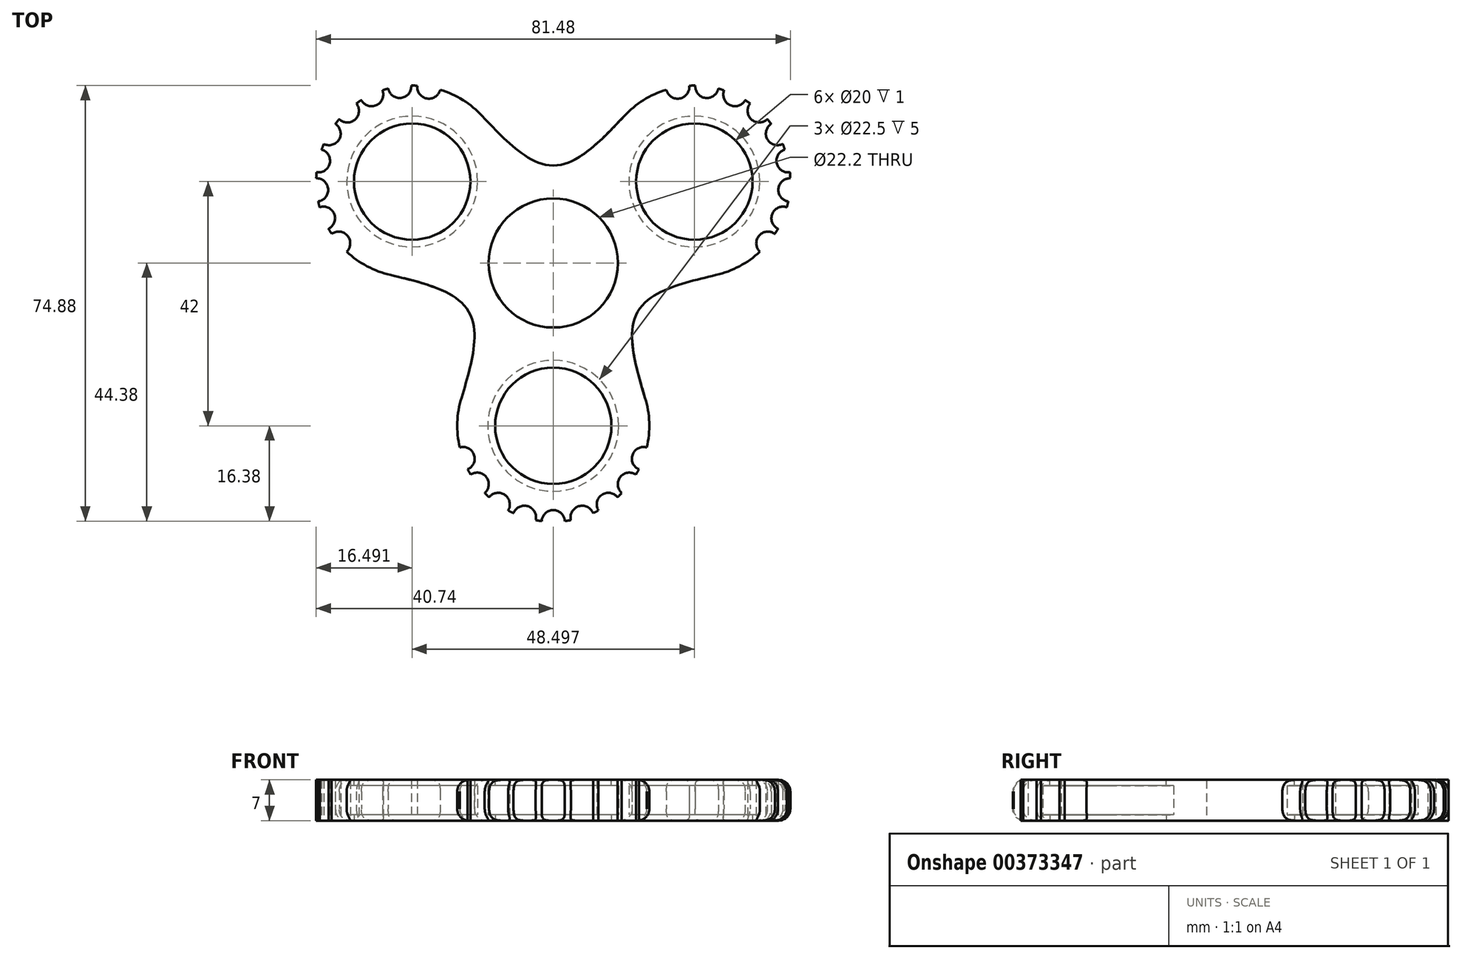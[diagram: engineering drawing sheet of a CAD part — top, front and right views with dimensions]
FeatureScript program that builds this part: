
annotation { "Feature Type Name" : "Feature", "Feature Type Description" : "" }
export const myFeature = defineFeature(function(context is Context, id is Id, definition is map)
    precondition{}
    {
        {
            var Q0;
            Q0=qCreatedBy(makeId("Top.planeOp"),FACE);
            var sketch = newSketch(context, id + "F0", { "sketchPlane" : qUnion([Q0])});
            skCircle(sketch, "E0", {"center": v(0, 0) * mm, "radius": 11.1 * mm});
            skCircle(sketch, "E1", {"center": v(-24.25, 14) * mm, "radius": 11.25 * mm});
            skCircle(sketch, "E2", {"center": v(24.25, 14) * mm, "radius": 11.25 * mm});
            skCircle(sketch, "E3", {"center": v(0, -28) * mm, "radius": 11.25 * mm});
            skLineSegment(sketch, "E4", {"start": v(-24.25, 14) * mm, "end": v(0, -28) * mm, "construction": true});
            skLineSegment(sketch, "E5", {"start": v(24.25, 14) * mm, "end": v(0, -28) * mm, "construction": true});
            skLineSegment(sketch, "E6", {"start": v(24.25, 14) * mm, "end": v(-24.25, 14) * mm, "construction": true});
            skLineSegment(sketch, "E7", {"start": v(0, 14) * mm, "end": v(0, 0) * mm, "construction": true});
            skLineSegment(sketch, "E8", {"start": v(0, 0) * mm, "end": v(12.12, -7) * mm, "construction": true});
            skLineSegment(sketch, "E9", {"start": v(0, 0) * mm, "end": v(-12.12, -7) * mm, "construction": true});
            skCircle(sketch, "E10", {"center": v(24.25, 14) * mm, "radius": 16.5 * mm});
            skCircle(sketch, "E11", {"center": v(-24.25, 14) * mm, "radius": 16.5 * mm});
            skCircle(sketch, "E12", {"center": v(0, -28) * mm, "radius": 16.5 * mm});
            skCircle(sketch, "E13", {"center": v(0, 0) * mm, "radius": 16.75 * mm, "construction": true});
            skLineSegment(sketch, "E14", {"start": v(-27.96, -2.08) * mm, "end": v(-15.78, -23.17) * mm, "construction": true});
            skLineSegment(sketch, "E15", {"start": v(15.78, -23.17) * mm, "end": v(27.96, -2.08) * mm, "construction": true});
            skLineSegment(sketch, "E16", {"start": v(12.18, 25.25) * mm, "end": v(-12.18, 25.25) * mm, "construction": true});
            skLineSegment(sketch, "E17", {"start": v(0, 0) * mm, "end": v(38.54, 22.25) * mm, "construction": true});
            skLineSegment(sketch, "E18", {"start": v(24.25, 14) * mm, "end": v(21.38, 30.25) * mm, "construction": true});
            skCircle(sketch, "E19", {"center": v(21.38, 30.25) * mm, "radius": 2 * mm});
            skCircle(sketch, "E20.1.0", {"center": v(26.4, 30.36) * mm, "radius": 2 * mm});
            skCircle(sketch, "E20.2.0", {"center": v(31.22, 28.95) * mm, "radius": 2 * mm});
            skCircle(sketch, "E20.3.0", {"center": v(35.4, 26.17) * mm, "radius": 2 * mm});
            skCircle(sketch, "E20.4.0", {"center": v(38.54, 22.25) * mm, "radius": 2 * mm});
            skCircle(sketch, "E20.5.0", {"center": v(40.36, 17.57) * mm, "radius": 2 * mm});
            skLineSegment(sketch, "E20.anchor2", {"start": v(24.25, 14) * mm, "end": v(36.89, 3.4) * mm, "construction": true});
            skCircle(sketch, "E21.1.0", {"center": v(-36.89, 3.4) * mm, "radius": 2 * mm});
            skCircle(sketch, "E21.1.1", {"center": v(-39.5, 7.69) * mm, "radius": 2 * mm});
            skCircle(sketch, "E21.1.2", {"center": v(-40.69, 12.56) * mm, "radius": 2 * mm});
            skCircle(sketch, "E21.1.3", {"center": v(-40.36, 17.57) * mm, "radius": 2 * mm});
            skCircle(sketch, "E21.1.4", {"center": v(-38.54, 22.25) * mm, "radius": 2 * mm});
            skCircle(sketch, "E21.1.5", {"center": v(-21.38, 30.25) * mm, "radius": 2 * mm});
            skCircle(sketch, "E21.2.0", {"center": v(15.5, -33.64) * mm, "radius": 2 * mm});
            skCircle(sketch, "E21.2.1", {"center": v(13.1, -38.04) * mm, "radius": 2 * mm});
            skCircle(sketch, "E21.2.2", {"center": v(9.46, -41.52) * mm, "radius": 2 * mm});
            skCircle(sketch, "E21.2.3", {"center": v(4.96, -43.74) * mm, "radius": 2 * mm});
            skCircle(sketch, "E21.2.4", {"center": v(0, -44.5) * mm, "radius": 2 * mm});
            skCircle(sketch, "E21.2.5", {"center": v(-15.5, -33.64) * mm, "radius": 2 * mm});
            skCircle(sketch, "E22", {"center": v(24.25, 14) * mm, "radius": 10 * mm});
            skCircle(sketch, "E23", {"center": v(0, -28) * mm, "radius": 10 * mm});
            skCircle(sketch, "E24", {"center": v(-24.25, 14) * mm, "radius": 10 * mm});
            skLineSegment(sketch, "E25", {"start": v(12.12, -7) * mm, "end": v(14.5, -8.38) * mm});
            skFitSpline(sketch, "E26", {"points": [v(27.96, -2.08) * mm, v(14.5, -8.38) * mm, v(15.78, -23.17) * mm], "startDerivative": vector(-34.36, -7.92) * mm, "endDerivative": vector(10.32, -33.72) * mm});
            skLineSegment(sketch, "E27", {"start": v(0, 14) * mm, "end": v(0, 16.75) * mm});
            skLineSegment(sketch, "E28", {"start": v(-12.12, -7) * mm, "end": v(-14.5, -8.38) * mm});
            skFitSpline(sketch, "E29", {"points": [v(-27.96, -2.08) * mm, v(-14.5, -8.37) * mm, v(-15.78, -23.17) * mm], "startDerivative": vector(34.36, -7.92) * mm, "endDerivative": vector(-10.32, -33.72) * mm});
            skFitSpline(sketch, "E30", {"points": [v(-12.18, 25.25) * mm, v(0, 16.75) * mm, v(12.18, 25.25) * mm], "startDerivative": vector(24.04, -25.8) * mm, "endDerivative": vector(24.04, 25.8) * mm});
            skCircle(sketch, "E31.1.6.0", {"center": v(40.69, 12.56) * mm, "radius": 2 * mm});
            skCircle(sketch, "E31.1.7.0", {"center": v(39.5, 7.69) * mm, "radius": 2 * mm});
            skCircle(sketch, "E31.1.8.0", {"center": v(36.89, 3.4) * mm, "radius": 2 * mm});
            skCircle(sketch, "E32.1.2", {"center": v(-26.4, 30.36) * mm, "radius": 2 * mm});
            skCircle(sketch, "E32.1.3", {"center": v(-31.22, 28.95) * mm, "radius": 2 * mm});
            skCircle(sketch, "E32.1.4", {"center": v(-35.4, 26.17) * mm, "radius": 2 * mm});
            skCircle(sketch, "E32.2.2", {"center": v(-13.1, -38.04) * mm, "radius": 2 * mm});
            skCircle(sketch, "E32.2.3", {"center": v(-9.46, -41.52) * mm, "radius": 2 * mm});
            skCircle(sketch, "E32.2.4", {"center": v(-4.96, -43.74) * mm, "radius": 2 * mm});
            skSolve(sketch);
        }
        {
            var Q0;
            Q0=makeQuery(id+"F0.imprint","IMPRINT",FACE,{"disambiguationData":[TD([[makeQuery(id+"F0.imprint","IMPRINT",EDGE,{"derivedFrom":sQuery(id+"F0.wireOp",EDGE,"E1")}),-1.0]])]});
            var Q1;
            Q1=makeQuery(id+"F0.imprint","IMPRINT",FACE,{"disambiguationData":[TD([[makeQuery(id+"F0.imprint","IMPRINT",EDGE,{"derivedFrom":sQuery(id+"F0.wireOp",EDGE,"E0")}),-1.0]])]});
            var Q2;
            Q2=makeQuery(id+"F0.imprint","IMPRINT",FACE,{"disambiguationData":[TD([[makeQuery(id+"F0.imprint","IMPRINT",EDGE,{"derivedFrom":sQuery(id+"F0.wireOp",EDGE,"E2")}),-1.0]])]});
            var Q3;
            Q3=makeQuery(id+"F0.imprint","IMPRINT",FACE,{"disambiguationData":[TD([[makeQuery(id+"F0.imprint","IMPRINT",EDGE,{"derivedFrom":sQuery(id+"F0.wireOp",EDGE,"E3")}),-1.0]])]});
            extrude(context, id + "F1", {"entities" : qUnion([Q0, Q1, Q2, Q3]), "depth" : 7 * mm});
        }
        {
            var Q0;
            Q0=makeQuery(id+"F0.imprint","IMPRINT",FACE,{"disambiguationData":[TD([[makeQuery(id+"F0.imprint","IMPRINT",EDGE,{"derivedFrom":sQuery(id+"F0.wireOp",EDGE,"E1")}),1.0]])]});
            var Q1;
            Q1=makeQuery(id+"F0.imprint","IMPRINT",FACE,{"disambiguationData":[TD([[makeQuery(id+"F0.imprint","IMPRINT",EDGE,{"derivedFrom":sQuery(id+"F0.wireOp",EDGE,"E2")}),1.0]])]});
            var Q2;
            Q2=makeQuery(id+"F0.imprint","IMPRINT",FACE,{"disambiguationData":[TD([[makeQuery(id+"F0.imprint","IMPRINT",EDGE,{"derivedFrom":sQuery(id+"F0.wireOp",EDGE,"E3")}),1.0]])]});
            extrude(context, id + "F2", {"entities" : qUnion([Q0, Q1, Q2]), "operationType" : NewBodyOperationType.ADD, "depth" : 1 * mm});
        }
        {
            var Q0;
            Q0=makeQuery(id+"F1.opExtrude","CAP_FACE",FACE,{"disambiguationData":[OSD([sQuery(id+"F0.wireOp",EDGE,"E0"),sQuery(id+"F0.wireOp",EDGE,"E1"),sQuery(id+"F0.wireOp",EDGE,"E2"),sQuery(id+"F0.wireOp",EDGE,"E3"),sQuery(id+"F0.wireOp",EDGE,"E10"),sQuery(id+"F0.wireOp",EDGE,"E11"),sQuery(id+"F0.wireOp",EDGE,"E12"),sQuery(id+"F0.wireOp",EDGE,"8c590d80-f1ca-4e74-8db3-8beb0ea57340"),sQuery(id+"F0.wireOp",EDGE,"774baf55-adde-4f7b-879e-53019140c20c"),sQuery(id+"F0.wireOp",EDGE,"c6e45883-406c-416c-8891-a9c8438ed052"),sQuery(id+"F0.wireOp",EDGE,"E19"),sQuery(id+"F0.wireOp",EDGE,"E20.1.0"),sQuery(id+"F0.wireOp",EDGE,"E20.2.0"),sQuery(id+"F0.wireOp",EDGE,"E20.3.0"),sQuery(id+"F0.wireOp",EDGE,"E20.4.0"),sQuery(id+"F0.wireOp",EDGE,"E20.5.0"),sQuery(id+"F0.wireOp",EDGE,"E21.1.0"),sQuery(id+"F0.wireOp",EDGE,"E21.1.1"),sQuery(id+"F0.wireOp",EDGE,"E21.1.2"),sQuery(id+"F0.wireOp",EDGE,"E21.1.3"),sQuery(id+"F0.wireOp",EDGE,"E21.1.4"),sQuery(id+"F0.wireOp",EDGE,"E21.1.5"),sQuery(id+"F0.wireOp",EDGE,"E21.2.0"),sQuery(id+"F0.wireOp",EDGE,"E21.2.1"),sQuery(id+"F0.wireOp",EDGE,"E21.2.2"),sQuery(id+"F0.wireOp",EDGE,"E21.2.3"),sQuery(id+"F0.wireOp",EDGE,"E21.2.4"),sQuery(id+"F0.wireOp",EDGE,"E21.2.5")])],"isStart":false});
            var sketch = newSketch(context, id + "F3", { "sketchPlane" : qUnion([Q0])});
            skCircle(sketch, "E33", {"center": v(-24.25, 14) * mm, "radius": 10 * mm});
            skCircle(sketch, "E34", {"center": v(0, -28) * mm, "radius": 10 * mm});
            skCircle(sketch, "E35", {"center": v(24.25, 14) * mm, "radius": 10 * mm});
            skSolve(sketch);
        }
        {
            var Q0;
            Q0=makeQuery(id+"F3.imprint","IMPRINT",FACE,{"disambiguationData":[TD([[makeQuery(id+"F3.imprint","IMPRINT",EDGE,{"derivedFrom":sQuery(id+"F3.wireOp",EDGE,"E35")}),-1.0]])]});
            var Q1;
            Q1=makeQuery(id+"F3.imprint","IMPRINT",FACE,{"disambiguationData":[TD([[makeQuery(id+"F3.imprint","IMPRINT",EDGE,{"derivedFrom":sQuery(id+"F3.wireOp",EDGE,"E34")}),-1.0]])]});
            var Q2;
            Q2=makeQuery(id+"F3.imprint","IMPRINT",FACE,{"disambiguationData":[TD([[makeQuery(id+"F3.imprint","IMPRINT",EDGE,{"derivedFrom":sQuery(id+"F3.wireOp",EDGE,"E33")}),-1.0]])]});
            extrude(context, id + "F4", {"entities" : qUnion([Q0, Q1, Q2]), "operationType" : NewBodyOperationType.ADD, "depth" : -1 * mm});
        }
        {
            var Q0;
            {var subQ0=sQuery(id+"F0.wireOp",EDGE,"E11");Q0=makeQuery(id+"F1.opExtrude","CAP_EDGE",EDGE,{"disambiguationData":[OSD([subQ0]),TDD([makeQuery(id+"F0.imprint","IMPRINT",EDGE,{"disambiguationData":[TD([[makeQuery(id+"F0.imprint","INTERSECT",VERTEX,{"derivedFrom":[subQ0,sQuery(id+"F0.wireOp",EDGE,"E29")]}),1.0]])],"derivedFrom":subQ0})])],"isStart":true});}
            var Q1;
            Q1=makeQuery(id+"F1.opExtrude","CAP_EDGE",EDGE,{"disambiguationData":[OSD([sQuery(id+"F0.wireOp",EDGE,"E29")])],"isStart":true});
            var Q2;
            {var subQ0=sQuery(id+"F0.wireOp",EDGE,"E12");Q2=makeQuery(id+"F1.opExtrude","CAP_EDGE",EDGE,{"disambiguationData":[OSD([subQ0]),TDD([makeQuery(id+"F0.imprint","IMPRINT",EDGE,{"disambiguationData":[TD([[makeQuery(id+"F0.imprint","INTERSECT",VERTEX,{"derivedFrom":[subQ0,sQuery(id+"F0.wireOp",EDGE,"E29")]}),-1.0]])],"derivedFrom":subQ0})])],"isStart":true});}
            var Q3;
            {var subQ0=sQuery(id+"F0.wireOp",EDGE,"E12");Q3=makeQuery(id+"F1.opExtrude","CAP_EDGE",EDGE,{"disambiguationData":[OSD([subQ0]),TDD([makeQuery(id+"F0.imprint","IMPRINT",EDGE,{"disambiguationData":[TD([[makeQuery(id+"F0.imprint","INTERSECT",VERTEX,{"derivedFrom":[subQ0,sQuery(id+"F0.wireOp",EDGE,"E26")]}),1.0]])],"derivedFrom":subQ0})])],"isStart":true});}
            var Q4;
            Q4=makeQuery(id+"F1.opExtrude","CAP_EDGE",EDGE,{"disambiguationData":[OSD([sQuery(id+"F0.wireOp",EDGE,"E26")])],"isStart":true});
            var Q5;
            {var subQ0=sQuery(id+"F0.wireOp",EDGE,"E10");Q5=makeQuery(id+"F1.opExtrude","CAP_EDGE",EDGE,{"disambiguationData":[OSD([subQ0]),TDD([makeQuery(id+"F0.imprint","IMPRINT",EDGE,{"disambiguationData":[TD([[makeQuery(id+"F0.imprint","INTERSECT",VERTEX,{"derivedFrom":[subQ0,sQuery(id+"F0.wireOp",EDGE,"E26")]}),-1.0]])],"derivedFrom":subQ0})])],"isStart":true});}
            var Q6;
            {var subQ0=sQuery(id+"F0.wireOp",EDGE,"E10");Q6=makeQuery(id+"F1.opExtrude","CAP_EDGE",EDGE,{"disambiguationData":[OSD([subQ0]),TDD([makeQuery(id+"F0.imprint","IMPRINT",EDGE,{"disambiguationData":[TD([[makeQuery(id+"F0.imprint","INTERSECT",VERTEX,{"disambiguationData":[OD(1.0)],"derivedFrom":[subQ0,sQuery(id+"F0.wireOp",EDGE,"E31.1.8.0")]}),-1.0]])],"derivedFrom":subQ0})])],"isStart":true});}
            var Q7;
            {var subQ0=sQuery(id+"F0.wireOp",EDGE,"E10");Q7=makeQuery(id+"F1.opExtrude","CAP_EDGE",EDGE,{"disambiguationData":[OSD([subQ0]),TDD([makeQuery(id+"F0.imprint","IMPRINT",EDGE,{"disambiguationData":[TD([[makeQuery(id+"F0.imprint","INTERSECT",VERTEX,{"disambiguationData":[OD(1.0)],"derivedFrom":[subQ0,sQuery(id+"F0.wireOp",EDGE,"E31.1.7.0")]}),-1.0]])],"derivedFrom":subQ0})])],"isStart":true});}
            var Q8;
            {var subQ0=sQuery(id+"F0.wireOp",EDGE,"E10");Q8=makeQuery(id+"F1.opExtrude","CAP_EDGE",EDGE,{"disambiguationData":[OSD([subQ0]),TDD([makeQuery(id+"F0.imprint","IMPRINT",EDGE,{"disambiguationData":[TD([[makeQuery(id+"F0.imprint","INTERSECT",VERTEX,{"disambiguationData":[OD(0.0)],"derivedFrom":[subQ0,sQuery(id+"F0.wireOp",EDGE,"E20.5.0")]}),1.0]])],"derivedFrom":subQ0})])],"isStart":true});}
            var Q9;
            {var subQ0=sQuery(id+"F0.wireOp",EDGE,"E10");Q9=makeQuery(id+"F1.opExtrude","CAP_EDGE",EDGE,{"disambiguationData":[OSD([subQ0]),TDD([makeQuery(id+"F0.imprint","IMPRINT",EDGE,{"disambiguationData":[TD([[makeQuery(id+"F0.imprint","INTERSECT",VERTEX,{"disambiguationData":[OD(1.0)],"derivedFrom":[subQ0,sQuery(id+"F0.wireOp",EDGE,"E20.5.0")]}),-1.0]])],"derivedFrom":subQ0})])],"isStart":true});}
            var Q10;
            {var subQ0=sQuery(id+"F0.wireOp",EDGE,"E10");Q10=makeQuery(id+"F1.opExtrude","CAP_EDGE",EDGE,{"disambiguationData":[OSD([subQ0]),TDD([makeQuery(id+"F0.imprint","IMPRINT",EDGE,{"disambiguationData":[TD([[makeQuery(id+"F0.imprint","INTERSECT",VERTEX,{"disambiguationData":[OD(1.0)],"derivedFrom":[subQ0,sQuery(id+"F0.wireOp",EDGE,"E20.4.0")]}),-1.0]])],"derivedFrom":subQ0})])],"isStart":true});}
            var Q11;
            {var subQ0=sQuery(id+"F0.wireOp",EDGE,"E10");Q11=makeQuery(id+"F1.opExtrude","CAP_EDGE",EDGE,{"disambiguationData":[OSD([subQ0]),TDD([makeQuery(id+"F0.imprint","IMPRINT",EDGE,{"disambiguationData":[TD([[makeQuery(id+"F0.imprint","INTERSECT",VERTEX,{"disambiguationData":[OD(1.0)],"derivedFrom":[subQ0,sQuery(id+"F0.wireOp",EDGE,"E20.3.0")]}),-1.0]])],"derivedFrom":subQ0})])],"isStart":true});}
            var Q12;
            {var subQ0=sQuery(id+"F0.wireOp",EDGE,"E10");Q12=makeQuery(id+"F1.opExtrude","CAP_EDGE",EDGE,{"disambiguationData":[OSD([subQ0]),TDD([makeQuery(id+"F0.imprint","IMPRINT",EDGE,{"disambiguationData":[TD([[makeQuery(id+"F0.imprint","INTERSECT",VERTEX,{"disambiguationData":[OD(1.0)],"derivedFrom":[subQ0,sQuery(id+"F0.wireOp",EDGE,"E20.2.0")]}),-1.0]])],"derivedFrom":subQ0})])],"isStart":true});}
            var Q13;
            {var subQ0=sQuery(id+"F0.wireOp",EDGE,"E10");Q13=makeQuery(id+"F1.opExtrude","CAP_EDGE",EDGE,{"disambiguationData":[OSD([subQ0]),TDD([makeQuery(id+"F0.imprint","IMPRINT",EDGE,{"disambiguationData":[TD([[makeQuery(id+"F0.imprint","INTERSECT",VERTEX,{"disambiguationData":[OD(1.0)],"derivedFrom":[subQ0,sQuery(id+"F0.wireOp",EDGE,"E20.1.0")]}),-1.0]])],"derivedFrom":subQ0})])],"isStart":true});}
            var Q14;
            {var subQ0=sQuery(id+"F0.wireOp",EDGE,"E10");Q14=makeQuery(id+"F1.opExtrude","CAP_EDGE",EDGE,{"disambiguationData":[OSD([subQ0]),TDD([makeQuery(id+"F0.imprint","IMPRINT",EDGE,{"disambiguationData":[TD([[makeQuery(id+"F0.imprint","INTERSECT",VERTEX,{"derivedFrom":[subQ0,sQuery(id+"F0.wireOp",EDGE,"E30")]}),1.0]])],"derivedFrom":subQ0})])],"isStart":true});}
            var Q15;
            {var subQ0=sQuery(id+"F0.wireOp",EDGE,"E11");Q15=makeQuery(id+"F1.opExtrude","CAP_EDGE",EDGE,{"disambiguationData":[OSD([subQ0]),TDD([makeQuery(id+"F0.imprint","IMPRINT",EDGE,{"disambiguationData":[TD([[makeQuery(id+"F0.imprint","INTERSECT",VERTEX,{"disambiguationData":[OD(1.0)],"derivedFrom":[subQ0,sQuery(id+"F0.wireOp",EDGE,"E21.1.5")]}),-1.0]])],"derivedFrom":subQ0})])],"isStart":true});}
            var Q16;
            {var subQ0=sQuery(id+"F0.wireOp",EDGE,"E11");Q16=makeQuery(id+"F1.opExtrude","CAP_EDGE",EDGE,{"disambiguationData":[OSD([subQ0]),TDD([makeQuery(id+"F0.imprint","IMPRINT",EDGE,{"disambiguationData":[TD([[makeQuery(id+"F0.imprint","INTERSECT",VERTEX,{"disambiguationData":[OD(1.0)],"derivedFrom":[subQ0,sQuery(id+"F0.wireOp",EDGE,"E32.1.2")]}),-1.0]])],"derivedFrom":subQ0})])],"isStart":true});}
            var Q17;
            {var subQ0=sQuery(id+"F0.wireOp",EDGE,"E11");Q17=makeQuery(id+"F1.opExtrude","CAP_EDGE",EDGE,{"disambiguationData":[OSD([subQ0]),TDD([makeQuery(id+"F0.imprint","IMPRINT",EDGE,{"disambiguationData":[TD([[makeQuery(id+"F0.imprint","INTERSECT",VERTEX,{"disambiguationData":[OD(1.0)],"derivedFrom":[subQ0,sQuery(id+"F0.wireOp",EDGE,"E32.1.3")]}),-1.0]])],"derivedFrom":subQ0})])],"isStart":true});}
            var Q18;
            {var subQ0=sQuery(id+"F0.wireOp",EDGE,"E11");Q18=makeQuery(id+"F1.opExtrude","CAP_EDGE",EDGE,{"disambiguationData":[OSD([subQ0]),TDD([makeQuery(id+"F0.imprint","IMPRINT",EDGE,{"disambiguationData":[TD([[makeQuery(id+"F0.imprint","INTERSECT",VERTEX,{"disambiguationData":[OD(1.0)],"derivedFrom":[subQ0,sQuery(id+"F0.wireOp",EDGE,"E32.1.4")]}),-1.0]])],"derivedFrom":subQ0})])],"isStart":true});}
            var Q19;
            {var subQ0=sQuery(id+"F0.wireOp",EDGE,"E11");Q19=makeQuery(id+"F1.opExtrude","CAP_EDGE",EDGE,{"disambiguationData":[OSD([subQ0]),TDD([makeQuery(id+"F0.imprint","IMPRINT",EDGE,{"disambiguationData":[TD([[makeQuery(id+"F0.imprint","INTERSECT",VERTEX,{"disambiguationData":[OD(1.0)],"derivedFrom":[subQ0,sQuery(id+"F0.wireOp",EDGE,"E21.1.4")]}),-1.0]])],"derivedFrom":subQ0})])],"isStart":true});}
            var Q20;
            {var subQ0=sQuery(id+"F0.wireOp",EDGE,"E11");Q20=makeQuery(id+"F1.opExtrude","CAP_EDGE",EDGE,{"disambiguationData":[OSD([subQ0]),TDD([makeQuery(id+"F0.imprint","IMPRINT",EDGE,{"disambiguationData":[TD([[makeQuery(id+"F0.imprint","INTERSECT",VERTEX,{"disambiguationData":[OD(1.0)],"derivedFrom":[subQ0,sQuery(id+"F0.wireOp",EDGE,"E21.1.3")]}),-1.0]])],"derivedFrom":subQ0})])],"isStart":true});}
            var Q21;
            {var subQ0=sQuery(id+"F0.wireOp",EDGE,"E11");Q21=makeQuery(id+"F1.opExtrude","CAP_EDGE",EDGE,{"disambiguationData":[OSD([subQ0]),TDD([makeQuery(id+"F0.imprint","IMPRINT",EDGE,{"disambiguationData":[TD([[makeQuery(id+"F0.imprint","INTERSECT",VERTEX,{"disambiguationData":[OD(1.0)],"derivedFrom":[subQ0,sQuery(id+"F0.wireOp",EDGE,"E21.1.2")]}),-1.0]])],"derivedFrom":subQ0})])],"isStart":true});}
            var Q22;
            {var subQ0=sQuery(id+"F0.wireOp",EDGE,"E11");Q22=makeQuery(id+"F1.opExtrude","CAP_EDGE",EDGE,{"disambiguationData":[OSD([subQ0]),TDD([makeQuery(id+"F0.imprint","IMPRINT",EDGE,{"disambiguationData":[TD([[makeQuery(id+"F0.imprint","INTERSECT",VERTEX,{"disambiguationData":[OD(1.0)],"derivedFrom":[subQ0,sQuery(id+"F0.wireOp",EDGE,"E21.1.1")]}),-1.0]])],"derivedFrom":subQ0})])],"isStart":true});}
            var Q23;
            {var subQ0=sQuery(id+"F0.wireOp",EDGE,"E12");Q23=makeQuery(id+"F1.opExtrude","CAP_EDGE",EDGE,{"disambiguationData":[OSD([subQ0]),TDD([makeQuery(id+"F0.imprint","IMPRINT",EDGE,{"disambiguationData":[TD([[makeQuery(id+"F0.imprint","INTERSECT",VERTEX,{"disambiguationData":[OD(1.0)],"derivedFrom":[subQ0,sQuery(id+"F0.wireOp",EDGE,"E21.2.1")]}),-1.0]])],"derivedFrom":subQ0})])],"isStart":true});}
            var Q24;
            {var subQ0=sQuery(id+"F0.wireOp",EDGE,"E12");Q24=makeQuery(id+"F1.opExtrude","CAP_EDGE",EDGE,{"disambiguationData":[OSD([subQ0]),TDD([makeQuery(id+"F0.imprint","IMPRINT",EDGE,{"disambiguationData":[TD([[makeQuery(id+"F0.imprint","INTERSECT",VERTEX,{"disambiguationData":[OD(1.0)],"derivedFrom":[subQ0,sQuery(id+"F0.wireOp",EDGE,"E21.2.2")]}),-1.0]])],"derivedFrom":subQ0})])],"isStart":true});}
            var Q25;
            {var subQ0=sQuery(id+"F0.wireOp",EDGE,"E12");Q25=makeQuery(id+"F1.opExtrude","CAP_EDGE",EDGE,{"disambiguationData":[OSD([subQ0]),TDD([makeQuery(id+"F0.imprint","IMPRINT",EDGE,{"disambiguationData":[TD([[makeQuery(id+"F0.imprint","INTERSECT",VERTEX,{"disambiguationData":[OD(1.0)],"derivedFrom":[subQ0,sQuery(id+"F0.wireOp",EDGE,"E21.2.3")]}),-1.0]])],"derivedFrom":subQ0})])],"isStart":true});}
            var Q26;
            {var subQ0=sQuery(id+"F0.wireOp",EDGE,"E12");Q26=makeQuery(id+"F1.opExtrude","CAP_EDGE",EDGE,{"disambiguationData":[OSD([subQ0]),TDD([makeQuery(id+"F0.imprint","IMPRINT",EDGE,{"disambiguationData":[TD([[makeQuery(id+"F0.imprint","INTERSECT",VERTEX,{"disambiguationData":[OD(1.0)],"derivedFrom":[subQ0,sQuery(id+"F0.wireOp",EDGE,"E21.2.4")]}),-1.0]])],"derivedFrom":subQ0})])],"isStart":true});}
            var Q27;
            {var subQ0=sQuery(id+"F0.wireOp",EDGE,"E12");Q27=makeQuery(id+"F1.opExtrude","CAP_EDGE",EDGE,{"disambiguationData":[OSD([subQ0]),TDD([makeQuery(id+"F0.imprint","IMPRINT",EDGE,{"disambiguationData":[TD([[makeQuery(id+"F0.imprint","INTERSECT",VERTEX,{"disambiguationData":[OD(1.0)],"derivedFrom":[subQ0,sQuery(id+"F0.wireOp",EDGE,"E32.2.4")]}),-1.0]])],"derivedFrom":subQ0})])],"isStart":true});}
            var Q28;
            {var subQ0=sQuery(id+"F0.wireOp",EDGE,"E12");Q28=makeQuery(id+"F1.opExtrude","CAP_EDGE",EDGE,{"disambiguationData":[OSD([subQ0]),TDD([makeQuery(id+"F0.imprint","IMPRINT",EDGE,{"disambiguationData":[TD([[makeQuery(id+"F0.imprint","INTERSECT",VERTEX,{"disambiguationData":[OD(1.0)],"derivedFrom":[subQ0,sQuery(id+"F0.wireOp",EDGE,"E32.2.3")]}),-1.0]])],"derivedFrom":subQ0})])],"isStart":true});}
            var Q29;
            {var subQ0=sQuery(id+"F0.wireOp",EDGE,"E12");Q29=makeQuery(id+"F1.opExtrude","CAP_EDGE",EDGE,{"disambiguationData":[OSD([subQ0]),TDD([makeQuery(id+"F0.imprint","IMPRINT",EDGE,{"disambiguationData":[TD([[makeQuery(id+"F0.imprint","INTERSECT",VERTEX,{"disambiguationData":[OD(1.0)],"derivedFrom":[subQ0,sQuery(id+"F0.wireOp",EDGE,"E32.2.2")]}),-1.0]])],"derivedFrom":subQ0})])],"isStart":true});}
            var Q30;
            {var subQ0=sQuery(id+"F0.wireOp",EDGE,"E12");Q30=makeQuery(id+"F1.opExtrude","CAP_EDGE",EDGE,{"disambiguationData":[OSD([subQ0]),TDD([makeQuery(id+"F0.imprint","IMPRINT",EDGE,{"disambiguationData":[TD([[makeQuery(id+"F0.imprint","INTERSECT",VERTEX,{"disambiguationData":[OD(1.0)],"derivedFrom":[subQ0,sQuery(id+"F0.wireOp",EDGE,"E21.2.5")]}),-1.0]])],"derivedFrom":subQ0})])],"isStart":true});}
            var Q31;
            Q31=makeQuery(id+"F1.opExtrude","CAP_EDGE",EDGE,{"disambiguationData":[OSD([sQuery(id+"F0.wireOp",EDGE,"E30")])],"isStart":false});
            var Q32;
            Q32=makeQuery(id+"F1.opExtrude","CAP_EDGE",EDGE,{"disambiguationData":[OSD([sQuery(id+"F0.wireOp",EDGE,"E29")])],"isStart":false});
            var Q33;
            Q33=makeQuery(id+"F1.opExtrude","CAP_EDGE",EDGE,{"disambiguationData":[OSD([sQuery(id+"F0.wireOp",EDGE,"E26")])],"isStart":false});
            var Q34;
            {var subQ0=sQuery(id+"F0.wireOp",EDGE,"E11");Q34=makeQuery(id+"F1.opExtrude","CAP_EDGE",EDGE,{"disambiguationData":[OSD([subQ0]),TDD([makeQuery(id+"F0.imprint","IMPRINT",EDGE,{"disambiguationData":[TD([[makeQuery(id+"F0.imprint","INTERSECT",VERTEX,{"disambiguationData":[OD(1.0)],"derivedFrom":[subQ0,sQuery(id+"F0.wireOp",EDGE,"E21.1.5")]}),-1.0]])],"derivedFrom":subQ0})])],"isStart":false});}
            var Q35;
            {var subQ0=sQuery(id+"F0.wireOp",EDGE,"E11");Q35=makeQuery(id+"F1.opExtrude","CAP_EDGE",EDGE,{"disambiguationData":[OSD([subQ0]),TDD([makeQuery(id+"F0.imprint","IMPRINT",EDGE,{"disambiguationData":[TD([[makeQuery(id+"F0.imprint","INTERSECT",VERTEX,{"disambiguationData":[OD(1.0)],"derivedFrom":[subQ0,sQuery(id+"F0.wireOp",EDGE,"E32.1.2")]}),-1.0]])],"derivedFrom":subQ0})])],"isStart":false});}
            var Q36;
            {var subQ0=sQuery(id+"F0.wireOp",EDGE,"E11");Q36=makeQuery(id+"F1.opExtrude","CAP_EDGE",EDGE,{"disambiguationData":[OSD([subQ0]),TDD([makeQuery(id+"F0.imprint","IMPRINT",EDGE,{"disambiguationData":[TD([[makeQuery(id+"F0.imprint","INTERSECT",VERTEX,{"disambiguationData":[OD(1.0)],"derivedFrom":[subQ0,sQuery(id+"F0.wireOp",EDGE,"E32.1.3")]}),-1.0]])],"derivedFrom":subQ0})])],"isStart":false});}
            var Q37;
            {var subQ0=sQuery(id+"F0.wireOp",EDGE,"E11");Q37=makeQuery(id+"F1.opExtrude","CAP_EDGE",EDGE,{"disambiguationData":[OSD([subQ0]),TDD([makeQuery(id+"F0.imprint","IMPRINT",EDGE,{"disambiguationData":[TD([[makeQuery(id+"F0.imprint","INTERSECT",VERTEX,{"disambiguationData":[OD(1.0)],"derivedFrom":[subQ0,sQuery(id+"F0.wireOp",EDGE,"E32.1.4")]}),-1.0]])],"derivedFrom":subQ0})])],"isStart":false});}
            var Q38;
            {var subQ0=sQuery(id+"F0.wireOp",EDGE,"E11");Q38=makeQuery(id+"F1.opExtrude","CAP_EDGE",EDGE,{"disambiguationData":[OSD([subQ0]),TDD([makeQuery(id+"F0.imprint","IMPRINT",EDGE,{"disambiguationData":[TD([[makeQuery(id+"F0.imprint","INTERSECT",VERTEX,{"disambiguationData":[OD(1.0)],"derivedFrom":[subQ0,sQuery(id+"F0.wireOp",EDGE,"E21.1.4")]}),-1.0]])],"derivedFrom":subQ0})])],"isStart":false});}
            var Q39;
            {var subQ0=sQuery(id+"F0.wireOp",EDGE,"E11");Q39=makeQuery(id+"F1.opExtrude","CAP_EDGE",EDGE,{"disambiguationData":[OSD([subQ0]),TDD([makeQuery(id+"F0.imprint","IMPRINT",EDGE,{"disambiguationData":[TD([[makeQuery(id+"F0.imprint","INTERSECT",VERTEX,{"disambiguationData":[OD(1.0)],"derivedFrom":[subQ0,sQuery(id+"F0.wireOp",EDGE,"E21.1.3")]}),-1.0]])],"derivedFrom":subQ0})])],"isStart":false});}
            var Q40;
            {var subQ0=sQuery(id+"F0.wireOp",EDGE,"E11");Q40=makeQuery(id+"F1.opExtrude","CAP_EDGE",EDGE,{"disambiguationData":[OSD([subQ0]),TDD([makeQuery(id+"F0.imprint","IMPRINT",EDGE,{"disambiguationData":[TD([[makeQuery(id+"F0.imprint","INTERSECT",VERTEX,{"disambiguationData":[OD(1.0)],"derivedFrom":[subQ0,sQuery(id+"F0.wireOp",EDGE,"E21.1.2")]}),-1.0]])],"derivedFrom":subQ0})])],"isStart":false});}
            var Q41;
            {var subQ0=sQuery(id+"F0.wireOp",EDGE,"E11");Q41=makeQuery(id+"F1.opExtrude","CAP_EDGE",EDGE,{"disambiguationData":[OSD([subQ0]),TDD([makeQuery(id+"F0.imprint","IMPRINT",EDGE,{"disambiguationData":[TD([[makeQuery(id+"F0.imprint","INTERSECT",VERTEX,{"disambiguationData":[OD(1.0)],"derivedFrom":[subQ0,sQuery(id+"F0.wireOp",EDGE,"E21.1.1")]}),-1.0]])],"derivedFrom":subQ0})])],"isStart":false});}
            var Q42;
            {var subQ0=sQuery(id+"F0.wireOp",EDGE,"E10");Q42=makeQuery(id+"F1.opExtrude","CAP_EDGE",EDGE,{"disambiguationData":[OSD([subQ0]),TDD([makeQuery(id+"F0.imprint","IMPRINT",EDGE,{"disambiguationData":[TD([[makeQuery(id+"F0.imprint","INTERSECT",VERTEX,{"disambiguationData":[OD(1.0)],"derivedFrom":[subQ0,sQuery(id+"F0.wireOp",EDGE,"E20.1.0")]}),-1.0]])],"derivedFrom":subQ0})])],"isStart":false});}
            var Q43;
            {var subQ0=sQuery(id+"F0.wireOp",EDGE,"E10");Q43=makeQuery(id+"F1.opExtrude","CAP_EDGE",EDGE,{"disambiguationData":[OSD([subQ0]),TDD([makeQuery(id+"F0.imprint","IMPRINT",EDGE,{"disambiguationData":[TD([[makeQuery(id+"F0.imprint","INTERSECT",VERTEX,{"disambiguationData":[OD(1.0)],"derivedFrom":[subQ0,sQuery(id+"F0.wireOp",EDGE,"E20.2.0")]}),-1.0]])],"derivedFrom":subQ0})])],"isStart":false});}
            var Q44;
            {var subQ0=sQuery(id+"F0.wireOp",EDGE,"E10");Q44=makeQuery(id+"F1.opExtrude","CAP_EDGE",EDGE,{"disambiguationData":[OSD([subQ0]),TDD([makeQuery(id+"F0.imprint","IMPRINT",EDGE,{"disambiguationData":[TD([[makeQuery(id+"F0.imprint","INTERSECT",VERTEX,{"disambiguationData":[OD(1.0)],"derivedFrom":[subQ0,sQuery(id+"F0.wireOp",EDGE,"E20.3.0")]}),-1.0]])],"derivedFrom":subQ0})])],"isStart":false});}
            var Q45;
            {var subQ0=sQuery(id+"F0.wireOp",EDGE,"E10");Q45=makeQuery(id+"F1.opExtrude","CAP_EDGE",EDGE,{"disambiguationData":[OSD([subQ0]),TDD([makeQuery(id+"F0.imprint","IMPRINT",EDGE,{"disambiguationData":[TD([[makeQuery(id+"F0.imprint","INTERSECT",VERTEX,{"disambiguationData":[OD(1.0)],"derivedFrom":[subQ0,sQuery(id+"F0.wireOp",EDGE,"E20.4.0")]}),-1.0]])],"derivedFrom":subQ0})])],"isStart":false});}
            var Q46;
            {var subQ0=sQuery(id+"F0.wireOp",EDGE,"E10");Q46=makeQuery(id+"F1.opExtrude","CAP_EDGE",EDGE,{"disambiguationData":[OSD([subQ0]),TDD([makeQuery(id+"F0.imprint","IMPRINT",EDGE,{"disambiguationData":[TD([[makeQuery(id+"F0.imprint","INTERSECT",VERTEX,{"disambiguationData":[OD(1.0)],"derivedFrom":[subQ0,sQuery(id+"F0.wireOp",EDGE,"E20.5.0")]}),-1.0]])],"derivedFrom":subQ0})])],"isStart":false});}
            var Q47;
            {var subQ0=sQuery(id+"F0.wireOp",EDGE,"E10");Q47=makeQuery(id+"F1.opExtrude","CAP_EDGE",EDGE,{"disambiguationData":[OSD([subQ0]),TDD([makeQuery(id+"F0.imprint","IMPRINT",EDGE,{"disambiguationData":[TD([[makeQuery(id+"F0.imprint","INTERSECT",VERTEX,{"disambiguationData":[OD(0.0)],"derivedFrom":[subQ0,sQuery(id+"F0.wireOp",EDGE,"E20.5.0")]}),1.0]])],"derivedFrom":subQ0})])],"isStart":false});}
            var Q48;
            {var subQ0=sQuery(id+"F0.wireOp",EDGE,"E10");Q48=makeQuery(id+"F1.opExtrude","CAP_EDGE",EDGE,{"disambiguationData":[OSD([subQ0]),TDD([makeQuery(id+"F0.imprint","IMPRINT",EDGE,{"disambiguationData":[TD([[makeQuery(id+"F0.imprint","INTERSECT",VERTEX,{"disambiguationData":[OD(1.0)],"derivedFrom":[subQ0,sQuery(id+"F0.wireOp",EDGE,"E31.1.7.0")]}),-1.0]])],"derivedFrom":subQ0})])],"isStart":false});}
            var Q49;
            {var subQ0=sQuery(id+"F0.wireOp",EDGE,"E10");Q49=makeQuery(id+"F1.opExtrude","CAP_EDGE",EDGE,{"disambiguationData":[OSD([subQ0]),TDD([makeQuery(id+"F0.imprint","IMPRINT",EDGE,{"disambiguationData":[TD([[makeQuery(id+"F0.imprint","INTERSECT",VERTEX,{"disambiguationData":[OD(1.0)],"derivedFrom":[subQ0,sQuery(id+"F0.wireOp",EDGE,"E31.1.8.0")]}),-1.0]])],"derivedFrom":subQ0})])],"isStart":false});}
            var Q50;
            {var subQ0=sQuery(id+"F0.wireOp",EDGE,"E12");Q50=makeQuery(id+"F1.opExtrude","CAP_EDGE",EDGE,{"disambiguationData":[OSD([subQ0]),TDD([makeQuery(id+"F0.imprint","IMPRINT",EDGE,{"disambiguationData":[TD([[makeQuery(id+"F0.imprint","INTERSECT",VERTEX,{"disambiguationData":[OD(1.0)],"derivedFrom":[subQ0,sQuery(id+"F0.wireOp",EDGE,"E21.2.1")]}),-1.0]])],"derivedFrom":subQ0})])],"isStart":false});}
            var Q51;
            {var subQ0=sQuery(id+"F0.wireOp",EDGE,"E12");Q51=makeQuery(id+"F1.opExtrude","CAP_EDGE",EDGE,{"disambiguationData":[OSD([subQ0]),TDD([makeQuery(id+"F0.imprint","IMPRINT",EDGE,{"disambiguationData":[TD([[makeQuery(id+"F0.imprint","INTERSECT",VERTEX,{"disambiguationData":[OD(1.0)],"derivedFrom":[subQ0,sQuery(id+"F0.wireOp",EDGE,"E21.2.2")]}),-1.0]])],"derivedFrom":subQ0})])],"isStart":false});}
            var Q52;
            {var subQ0=sQuery(id+"F0.wireOp",EDGE,"E12");Q52=makeQuery(id+"F1.opExtrude","CAP_EDGE",EDGE,{"disambiguationData":[OSD([subQ0]),TDD([makeQuery(id+"F0.imprint","IMPRINT",EDGE,{"disambiguationData":[TD([[makeQuery(id+"F0.imprint","INTERSECT",VERTEX,{"disambiguationData":[OD(1.0)],"derivedFrom":[subQ0,sQuery(id+"F0.wireOp",EDGE,"E21.2.3")]}),-1.0]])],"derivedFrom":subQ0})])],"isStart":false});}
            var Q53;
            {var subQ0=sQuery(id+"F0.wireOp",EDGE,"E12");Q53=makeQuery(id+"F1.opExtrude","CAP_EDGE",EDGE,{"disambiguationData":[OSD([subQ0]),TDD([makeQuery(id+"F0.imprint","IMPRINT",EDGE,{"disambiguationData":[TD([[makeQuery(id+"F0.imprint","INTERSECT",VERTEX,{"disambiguationData":[OD(1.0)],"derivedFrom":[subQ0,sQuery(id+"F0.wireOp",EDGE,"E21.2.4")]}),-1.0]])],"derivedFrom":subQ0})])],"isStart":false});}
            var Q54;
            {var subQ0=sQuery(id+"F0.wireOp",EDGE,"E12");Q54=makeQuery(id+"F1.opExtrude","CAP_EDGE",EDGE,{"disambiguationData":[OSD([subQ0]),TDD([makeQuery(id+"F0.imprint","IMPRINT",EDGE,{"disambiguationData":[TD([[makeQuery(id+"F0.imprint","INTERSECT",VERTEX,{"disambiguationData":[OD(1.0)],"derivedFrom":[subQ0,sQuery(id+"F0.wireOp",EDGE,"E32.2.4")]}),-1.0]])],"derivedFrom":subQ0})])],"isStart":false});}
            var Q55;
            {var subQ0=sQuery(id+"F0.wireOp",EDGE,"E12");Q55=makeQuery(id+"F1.opExtrude","CAP_EDGE",EDGE,{"disambiguationData":[OSD([subQ0]),TDD([makeQuery(id+"F0.imprint","IMPRINT",EDGE,{"disambiguationData":[TD([[makeQuery(id+"F0.imprint","INTERSECT",VERTEX,{"disambiguationData":[OD(1.0)],"derivedFrom":[subQ0,sQuery(id+"F0.wireOp",EDGE,"E32.2.3")]}),-1.0]])],"derivedFrom":subQ0})])],"isStart":false});}
            var Q56;
            {var subQ0=sQuery(id+"F0.wireOp",EDGE,"E12");Q56=makeQuery(id+"F1.opExtrude","CAP_EDGE",EDGE,{"disambiguationData":[OSD([subQ0]),TDD([makeQuery(id+"F0.imprint","IMPRINT",EDGE,{"disambiguationData":[TD([[makeQuery(id+"F0.imprint","INTERSECT",VERTEX,{"disambiguationData":[OD(1.0)],"derivedFrom":[subQ0,sQuery(id+"F0.wireOp",EDGE,"E32.2.2")]}),-1.0]])],"derivedFrom":subQ0})])],"isStart":false});}
            var Q57;
            {var subQ0=sQuery(id+"F0.wireOp",EDGE,"E12");Q57=makeQuery(id+"F1.opExtrude","CAP_EDGE",EDGE,{"disambiguationData":[OSD([subQ0]),TDD([makeQuery(id+"F0.imprint","IMPRINT",EDGE,{"disambiguationData":[TD([[makeQuery(id+"F0.imprint","INTERSECT",VERTEX,{"disambiguationData":[OD(1.0)],"derivedFrom":[subQ0,sQuery(id+"F0.wireOp",EDGE,"E21.2.5")]}),-1.0]])],"derivedFrom":subQ0})])],"isStart":false});}
            fillet(context, id + "F5", {"entities" : qUnion([Q0, Q1, Q2, Q3, Q4, Q5, Q6, Q7, Q8, Q9, Q10, Q11, Q12, Q13, Q14, Q15, Q16, Q17, Q18, Q19, Q20, Q21, Q22, Q23, Q24, Q25, Q26, Q27, Q28, Q29, Q30, Q31, Q32, Q33, Q34, Q35, Q36, Q37, Q38, Q39, Q40, Q41, Q42, Q43, Q44, Q45, Q46, Q47, Q48, Q49, Q50, Q51, Q52, Q53, Q54, Q55, Q56, Q57]), "radius" : 2 * mm, "tangentPropagation" : true, "allowEdgeOverflow" : false});
        }
    });
